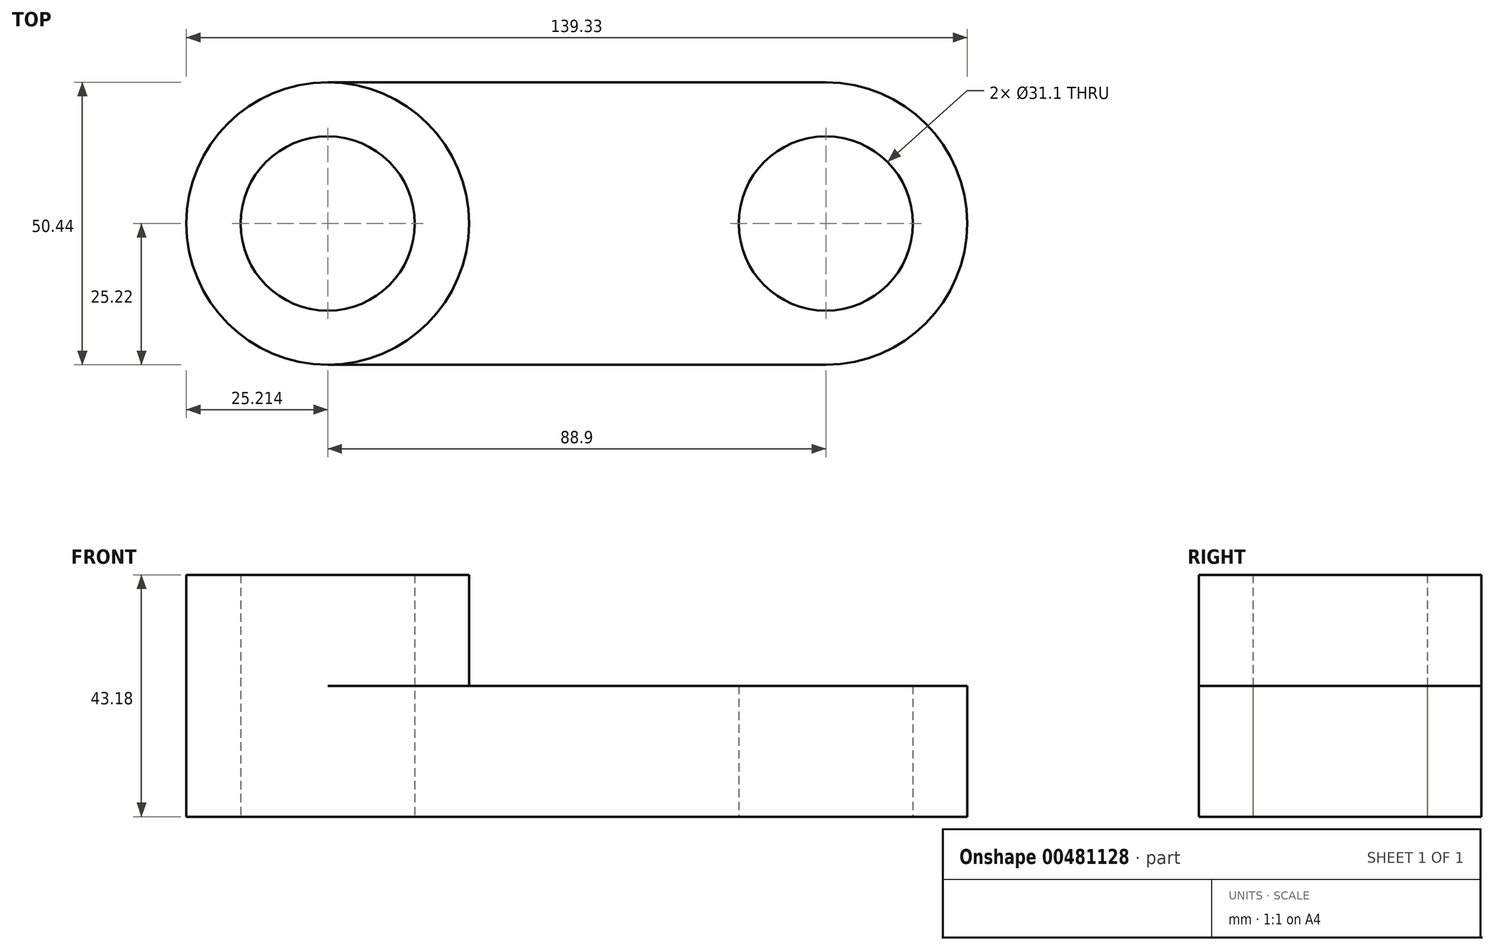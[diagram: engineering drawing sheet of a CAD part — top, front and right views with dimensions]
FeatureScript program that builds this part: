
annotation { "Feature Type Name" : "Feature", "Feature Type Description" : "" }
export const myFeature = defineFeature(function(context is Context, id is Id, definition is map)
    precondition{}
    {
        {
            var Q0;
            Q0=qCreatedBy(makeId("Top.planeOp"),FACE);
            var sketch = newSketch(context, id + "F0", { "sketchPlane" : qUnion([Q0])});
            skCircle(sketch, "E0", {"center": v(-48.85, 0) * mm, "radius": 25.22 * mm});
            skCircle(sketch, "E1", {"center": v(-48.85, 0) * mm, "radius": 15.55 * mm});
            skCircle(sketch, "E2", {"center": v(40.05, 0) * mm, "radius": 15.55 * mm});
            skLineSegment(sketch, "E3", {"start": v(-48.85, 25.22) * mm, "end": v(40.05, 25.22) * mm});
            skLineSegment(sketch, "E4", {"start": v(-48.85, -25.22) * mm, "end": v(40.05, -25.22) * mm});
            skArc(sketch, "E5", {"start": v(40.05, 25.22) * mm, "mid": v(65.27, 0) * mm, "end": v(40.05, -25.22) * mm});
            skSolve(sketch);
        }
        {
            var Q0;
            Q0=makeQuery(id+"F0.imprint","IMPRINT",FACE,{"disambiguationData":[TD([[makeQuery(id+"F0.imprint","IMPRINT",EDGE,{"derivedFrom":sQuery(id+"F0.wireOp",EDGE,"E1")}),-1.0]])]});
            extrude(context, id + "F1", {"entities" : qUnion([Q0]), "depth" : 43.18 * mm});
        }
        {
            var Q0;
            Q0 = qSketchRegion(id + "F0", true);
            extrude(context, id + "F2", {"entities" : qUnion([Q0]), "operationType" : NewBodyOperationType.ADD, "depth" : 23.37 * mm});
        }
    });
